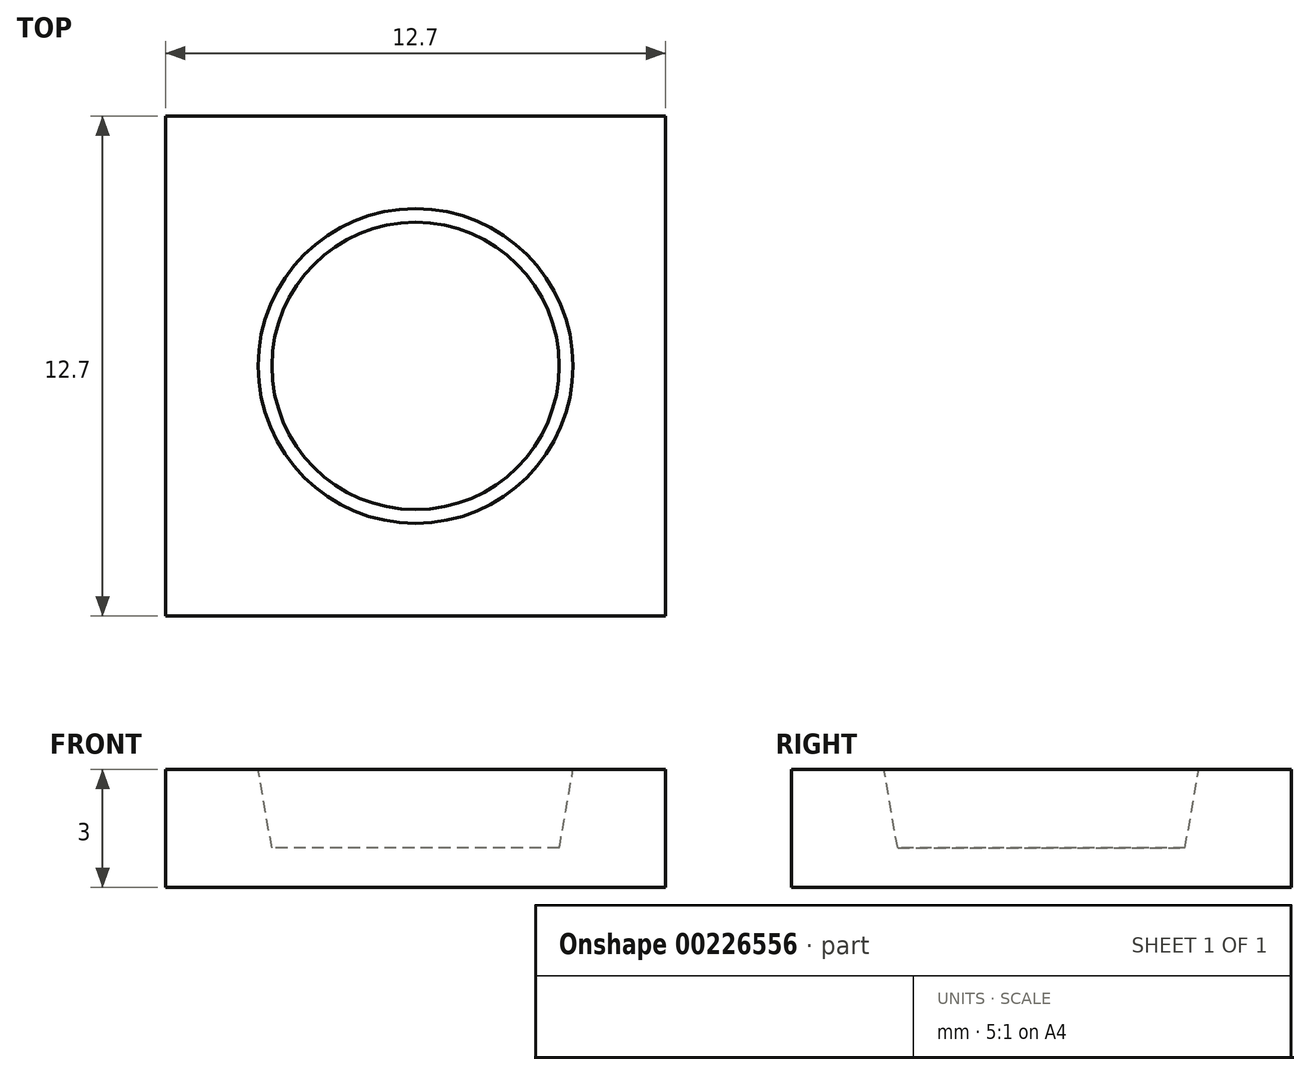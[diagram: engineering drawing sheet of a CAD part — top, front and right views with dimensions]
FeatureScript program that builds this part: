
annotation { "Feature Type Name" : "Feature", "Feature Type Description" : "" }
export const myFeature = defineFeature(function(context is Context, id is Id, definition is map)
    precondition{}
    {
        {
            var Q0;
            Q0=qCreatedBy(makeId("Top.planeOp"),FACE);
            var sketch = newSketch(context, id + "F0", { "sketchPlane" : qUnion([Q0])});
            skLineSegment(sketch, "E0.bottom", {"start": v(6.35, 6.35) * mm, "end": v(-6.35, 6.35) * mm});
            skLineSegment(sketch, "E0.top", {"start": v(6.35, -6.35) * mm, "end": v(-6.35, -6.35) * mm});
            skLineSegment(sketch, "E0.left", {"start": v(6.35, 6.35) * mm, "end": v(6.35, -6.35) * mm});
            skLineSegment(sketch, "E0.right", {"start": v(-6.35, 6.35) * mm, "end": v(-6.35, -6.35) * mm});
            skPoint(sketch, "E0.middle", {"position": v(0, 0) * mm});
            skSolve(sketch);
        }
        {
            var Q0;
            Q0=qSketchRegion(id+"F0",true);
            extrude(context, id + "F1", {"entities" : qUnion([Q0]), "depth" : 3 * mm});
        }
        {
            var Q0;
            Q0=makeQuery(id+"F1.opExtrude","CAP_FACE",FACE,{"disambiguationData":[OSD([sQuery(id+"F0.wireOp",EDGE,"E0.bottom"),sQuery(id+"F0.wireOp",EDGE,"E0.top"),sQuery(id+"F0.wireOp",EDGE,"E0.left"),sQuery(id+"F0.wireOp",EDGE,"E0.right")])],"isStart":false});
            var sketch = newSketch(context, id + "F2", { "sketchPlane" : qUnion([Q0])});
            skCircle(sketch, "E1", {"center": v(0, 0) * mm, "radius": 4 * mm});
            skSolve(sketch);
        }
        {
            var Q0;
            Q0=makeQuery(id+"F1.opExtrude","CAP_FACE",FACE,{"disambiguationData":[OSD([sQuery(id+"F0.wireOp",EDGE,"E0.bottom"),sQuery(id+"F0.wireOp",EDGE,"E0.top"),sQuery(id+"F0.wireOp",EDGE,"E0.left"),sQuery(id+"F0.wireOp",EDGE,"E0.right")])],"isStart":false});
            cPlane(context, id + "F3", {"entities" : qUnion([Q0]), "cplaneType" : CPlaneType.OFFSET, "offset" : 2 * mm, "oppositeDirection" : true, "width" : 150 * mm, "height" : 150 * mm});
        }
        {
            var Q0;
            Q0=qCreatedBy(id+"F3.planeOp",FACE);
            var sketch = newSketch(context, id + "F4", { "sketchPlane" : qUnion([Q0])});
            skCircle(sketch, "E2", {"center": v(0, 0) * mm, "radius": 3.65 * mm});
            skSolve(sketch);
        }
        {
            var Q0;
            Q0=makeQuery(id+"F2.imprint","IMPRINT",FACE,{"disambiguationData":[TD([[makeQuery(id+"F2.imprint","IMPRINT",EDGE,{"derivedFrom":sQuery(id+"F2.wireOp",EDGE,"E1")}),1.0]])]});
            var Q1;
            Q1=makeQuery(id+"F4.imprint","IMPRINT",FACE,{"disambiguationData":[TD([[makeQuery(id+"F4.imprint","IMPRINT",EDGE,{"derivedFrom":sQuery(id+"F4.wireOp",EDGE,"E2")}),1.0]])]});
            loft(context, id + "F5", {"operationType" : NewBodyOperationType.REMOVE, "sheetProfilesArray" : [{ "sheetProfileEntities" : qUnion([Q0]) }, { "sheetProfileEntities" : qUnion([Q1]) }]});
        }
    });
